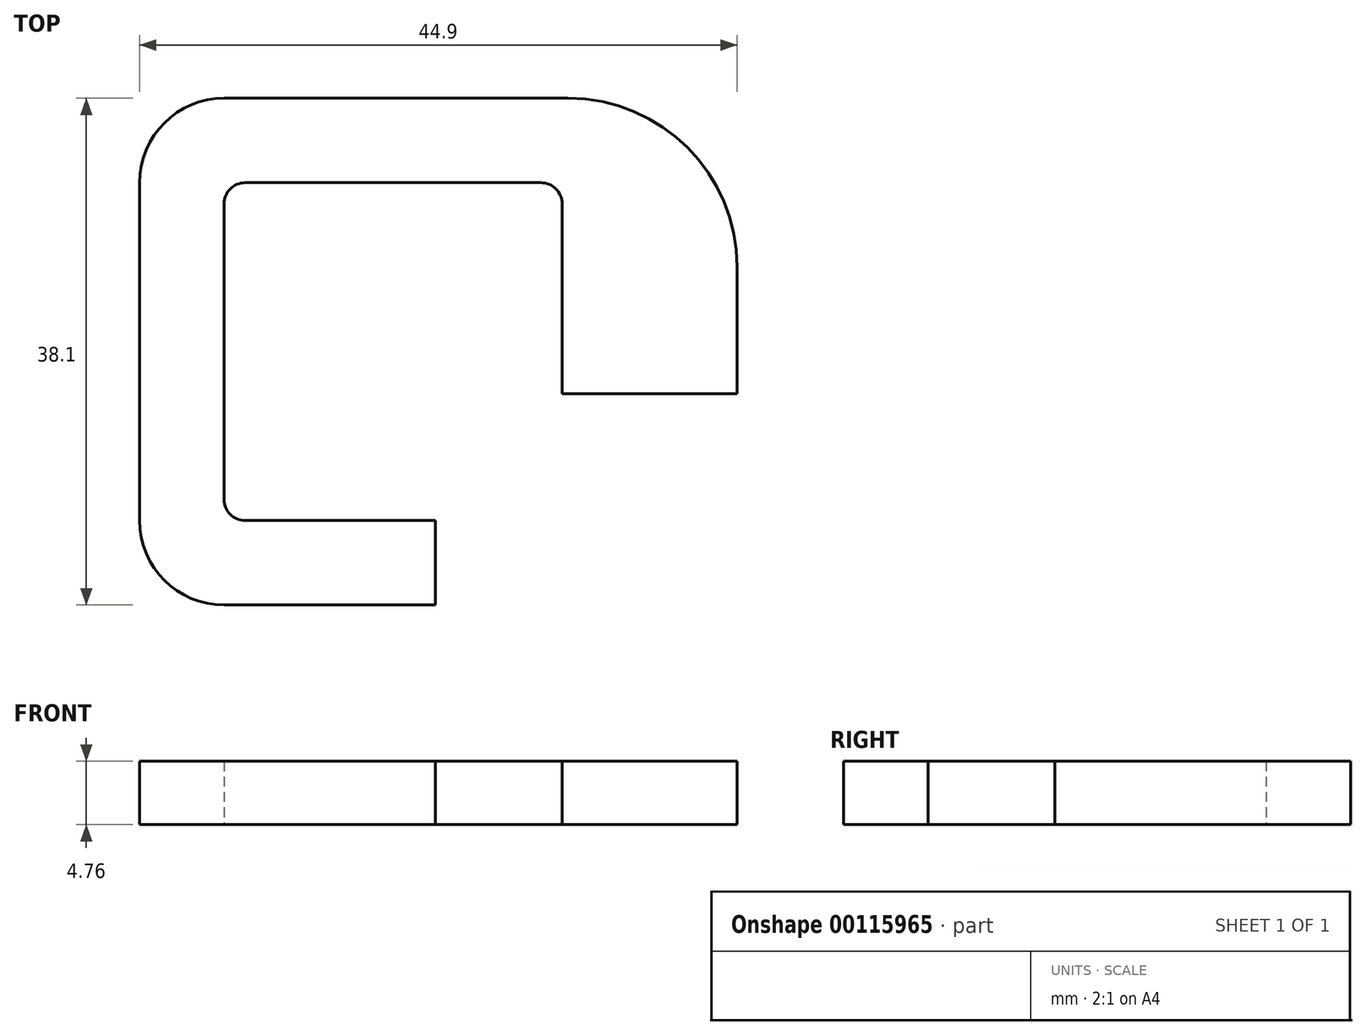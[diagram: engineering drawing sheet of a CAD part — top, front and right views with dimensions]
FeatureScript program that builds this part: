
annotation { "Feature Type Name" : "Feature", "Feature Type Description" : "" }
export const myFeature = defineFeature(function(context is Context, id is Id, definition is map)
    precondition{}
    {
        {
            var Q0;
            Q0=qCreatedBy(makeId("Top.planeOp"),FACE);
            var sketch = newSketch(context, id + "F0", { "sketchPlane" : qUnion([Q0])});
            skLineSegment(sketch, "E0.bottom", {"start": v(-30.44, -7.03) * mm, "end": v(-4.59, -7.03) * mm});
            skLineSegment(sketch, "E0.top", {"start": v(-30.44, -45.13) * mm, "end": v(-14.56, -45.13) * mm});
            skLineSegment(sketch, "E0.left", {"start": v(-36.79, -13.38) * mm, "end": v(-36.79, -38.78) * mm});
            skPoint(sketch, "E1.visualSharp", {"position": v(-36.79, -7.03) * mm});
            skArc(sketch, "E1.filletArc", {"start": v(-30.44, -7.03) * mm, "mid": v(-34.93, -8.89) * mm, "end": v(-36.79, -13.38) * mm});
            skPoint(sketch, "E2.visualSharp", {"position": v(1.31, -7.03) * mm});
            skPoint(sketch, "E3.visualSharp", {"position": v(-36.79, -45.13) * mm});
            skArc(sketch, "E3.filletArc", {"start": v(-36.79, -38.78) * mm, "mid": v(-34.93, -43.27) * mm, "end": v(-30.44, -45.13) * mm});
            skLineSegment(sketch, "E4.top", {"start": v(1.31, -29.25) * mm, "end": v(-5.04, -29.25) * mm});
            skLineSegment(sketch, "E4.right", {"start": v(-14.56, -45.13) * mm, "end": v(-14.56, -38.78) * mm});
            skLineSegment(sketch, "E5.bottom", {"start": v(-28.85, -13.38) * mm, "end": v(-6.63, -13.38) * mm});
            skLineSegment(sketch, "E5.top", {"start": v(-28.85, -38.78) * mm, "end": v(-14.56, -38.78) * mm});
            skLineSegment(sketch, "E5.left", {"start": v(-30.44, -14.97) * mm, "end": v(-30.44, -37.2) * mm});
            skLineSegment(sketch, "E5.right", {"start": v(-5.04, -14.97) * mm, "end": v(-5.04, -29.25) * mm});
            skPoint(sketch, "E6.visualSharp", {"position": v(-5.04, -13.38) * mm});
            skArc(sketch, "E6.filletArc", {"start": v(-5.04, -14.97) * mm, "mid": v(-5.5, -13.84) * mm, "end": v(-6.63, -13.38) * mm});
            skArc(sketch, "E7.filletArc", {"start": v(-28.85, -13.38) * mm, "mid": v(-29.97, -13.84) * mm, "end": v(-30.44, -14.97) * mm});
            skArc(sketch, "E8.filletArc", {"start": v(-30.44, -37.2) * mm, "mid": v(-29.97, -38.31) * mm, "end": v(-28.85, -38.78) * mm});
            skLineSegment(sketch, "E9", {"start": v(1.31, -29.25) * mm, "end": v(8.11, -29.25) * mm});
            skLineSegment(sketch, "E10", {"start": v(8.11, -29.25) * mm, "end": v(8.11, -19.73) * mm});
            skLineSegment(sketch, "E11", {"start": v(-4.59, -7.03) * mm, "end": v(-4.59, -7.03) * mm});
            skPoint(sketch, "E12.visualSharp", {"position": v(8.11, -7.03) * mm});
            skArc(sketch, "E12.filletArc", {"start": v(8.11, -19.73) * mm, "mid": v(4.4, -10.75) * mm, "end": v(-4.59, -7.03) * mm});
            skSolve(sketch);
        }
        {
            var Q0;
            Q0 = qSketchRegion(id + "F0", true);
            extrude(context, id + "F1", {"entities" : qUnion([Q0]), "endBound" : BoundingType.SYMMETRIC, "depth" : 4.76 * mm});
        }
    });
